# Revit family: Mixer-Sink-Caroma Skandic Care-240mm1
name_source: partatom
category: Plumbing Fixtures
revit_build: Autodesk Revit 2014 (Build: 20131024_2115(x64)
units: mm (PartAtom-declared; Revit-internal decimal feet)

## types (2) — shared parameters
Assembly Code = D2020300
CW Connection = Yes
CWFU = 1.98
Connector Radius = 10 mm  [stored 0.0328084 ft]
HW Connection = Yes
HWFU = 1.98
Height_ANZRS = 213 mm
Length_ANZRS = 59 mm
Manufacturer = GWA Bathrooms & Kitchens
Material_ANZRS = Metal-Chrome-Caroma
ModifiedIssue_ANZRS = 20150504 $
Pressure Drop = 0.00 psi
URL = http://specify.caroma.com.au
Vent Connection = No
WELSRating_ANZRS = WELS 4 Star rated, 7.5L/min
Waste Connection = No
Width_ANZRS = 275 mm
zero-valued in all types: Cost, Default Elevation

## per-type parameters (varying)
| type | Model | Type Comments | Warm |
| Hot/Cold | 90996C4A | Caroma Skandic Care Sink Mixer - Hot/Cold | No |
| Warm/Cold | 90999C4A | Caroma Skandic Care Sink Mixer - Warm/Cold | Yes |

note: [stored X ft] marks values corroborated as IEEE doubles in the binary element streams (Revit-internal decimal feet)

## geometry (parser evidence)
native form markers: Sweep x2
no freeform markers — native parametric forms only
